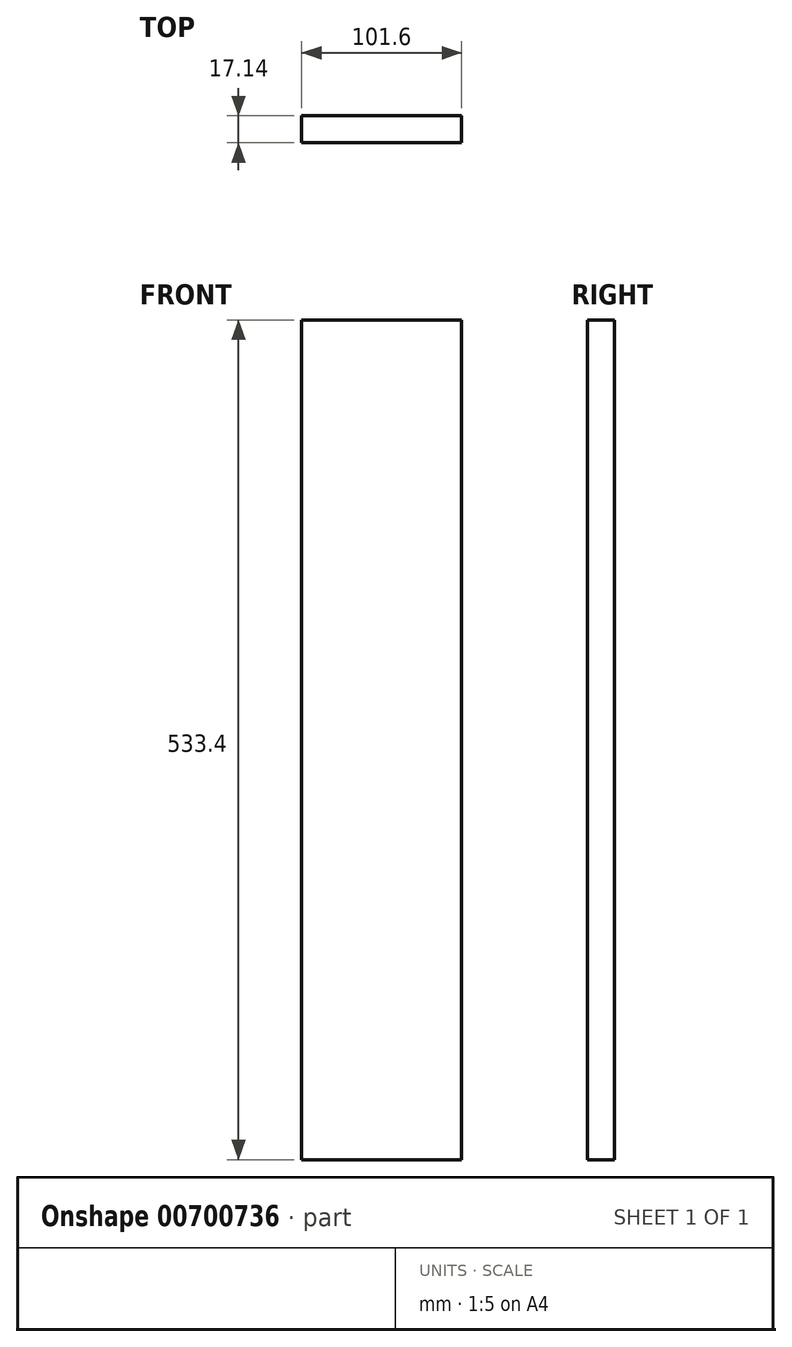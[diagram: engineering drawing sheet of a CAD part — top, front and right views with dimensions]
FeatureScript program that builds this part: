
annotation { "Feature Type Name" : "Feature", "Feature Type Description" : "" }
export const myFeature = defineFeature(function(context is Context, id is Id, definition is map)
    precondition{}
    {
        {
            var Q0;
            Q0=qCreatedBy(makeId("Front.planeOp"),FACE);
            var sketch = newSketch(context, id + "F0", { "sketchPlane" : qUnion([Q0])});
            skLineSegment(sketch, "E0.bottom", {"start": v(0, 0) * mm, "end": v(101.6, 0) * mm});
            skLineSegment(sketch, "E0.top", {"start": v(0, 533.4) * mm, "end": v(101.6, 533.4) * mm});
            skLineSegment(sketch, "E0.left", {"start": v(0, 0) * mm, "end": v(0, 533.4) * mm});
            skLineSegment(sketch, "E0.right", {"start": v(101.6, 0) * mm, "end": v(101.6, 533.4) * mm});
            skSolve(sketch);
        }
        {
            var Q0;
            Q0 = qSketchRegion(id + "F0", true);
            extrude(context, id + "F1", {"entities" : qUnion([Q0]), "depth" : 17.14 * mm, "offsetDistance" : 25.4 * mm});
        }
    });
